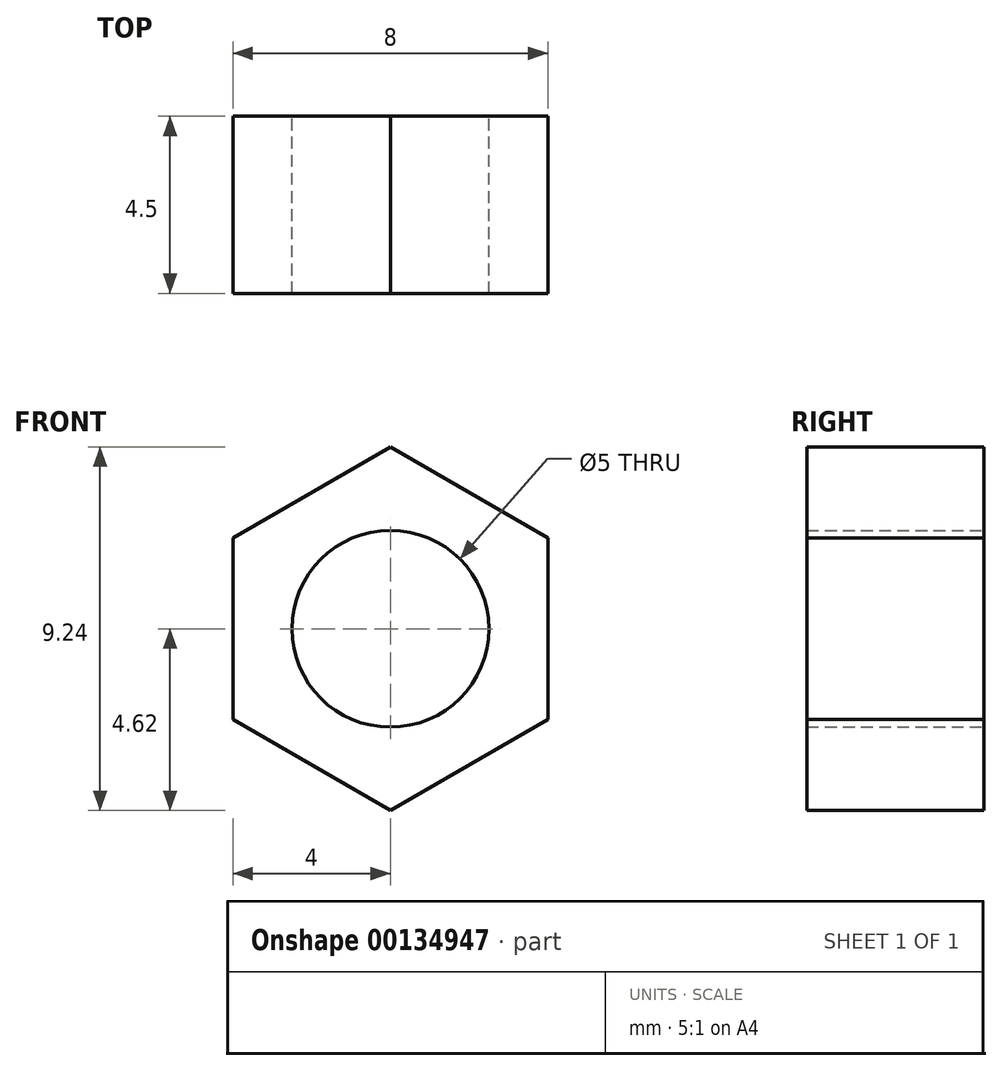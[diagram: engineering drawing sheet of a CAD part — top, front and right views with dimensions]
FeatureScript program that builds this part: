
annotation { "Feature Type Name" : "Feature", "Feature Type Description" : "" }
export const myFeature = defineFeature(function(context is Context, id is Id, definition is map)
    precondition{}
    {
        {
            var Q0;
            Q0=qCreatedBy(makeId("Front.planeOp"),FACE);
            var sketch = newSketch(context, id + "F0", { "sketchPlane" : qUnion([Q0])});
            skCircle(sketch, "E0.cCircle", {"center": v(0, 0) * mm, "radius": 4 * mm, "construction": true});
            skLineSegment(sketch, "E0.0", {"start": v(4, 2.3) * mm, "end": v(4, -2.3) * mm});
            skLineSegment(sketch, "E0.1", {"start": v(4, -2.3) * mm, "end": v(0, -4.62) * mm});
            skLineSegment(sketch, "E0.2", {"start": v(0, -4.62) * mm, "end": v(-4, -2.3) * mm});
            skLineSegment(sketch, "E0.3", {"start": v(-4, -2.3) * mm, "end": v(-4, 2.3) * mm});
            skLineSegment(sketch, "E0.4", {"start": v(-4, 2.3) * mm, "end": v(0, 4.62) * mm});
            skLineSegment(sketch, "E0.5", {"start": v(0, 4.62) * mm, "end": v(4, 2.3) * mm});
            skPoint(sketch, "E0.0.midPoint", {"position": v(4, 0) * mm});
            skCircle(sketch, "E1", {"center": v(0, 0) * mm, "radius": 2.5 * mm});
            skSolve(sketch);
        }
        {
            var Q0;
            Q0=makeQuery(id+"F0.imprint","IMPRINT",FACE,{"disambiguationData":[TD([[makeQuery(id+"F0.imprint","IMPRINT",EDGE,{"derivedFrom":sQuery(id+"F0.wireOp",EDGE,"E0.0")}),-1.0]])]});
            extrude(context, id + "F1", {"entities" : qUnion([Q0]), "depth" : 4.5 * mm});
        }
    });
